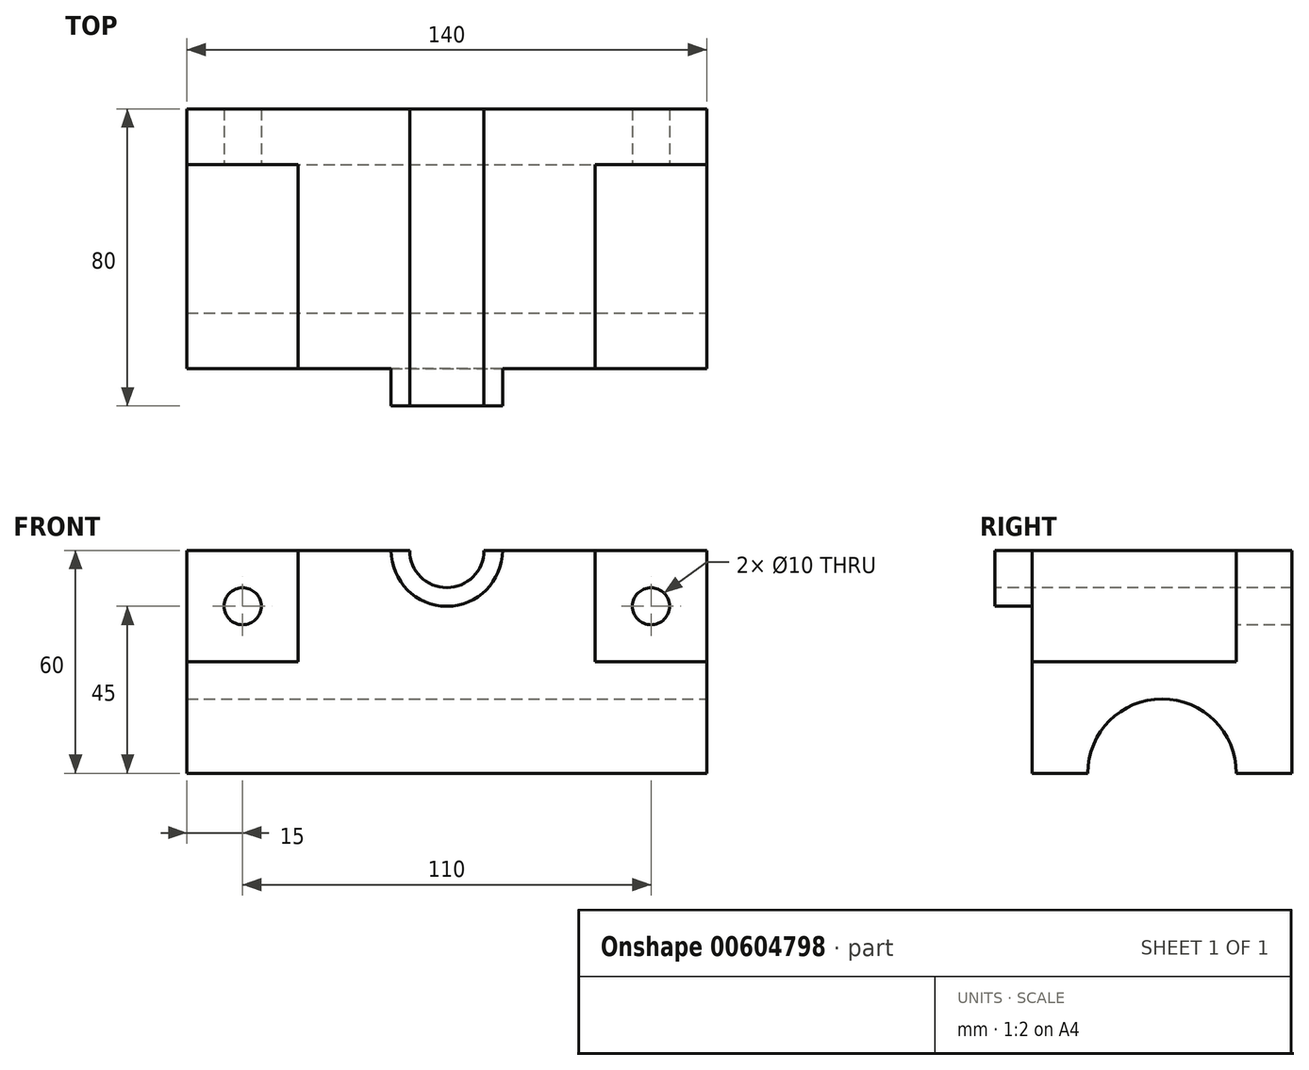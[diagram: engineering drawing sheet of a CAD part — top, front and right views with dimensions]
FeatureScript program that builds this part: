
annotation { "Feature Type Name" : "Feature", "Feature Type Description" : "" }
export const myFeature = defineFeature(function(context is Context, id is Id, definition is map)
    precondition{}
    {
        {
            var Q0;
            Q0=qCreatedBy(makeId("Front.planeOp"),FACE);
            var sketch = newSketch(context, id + "F0", { "sketchPlane" : qUnion([Q0])});
            skLineSegment(sketch, "E0.bottom", {"start": v(70, 30) * mm, "end": v(-70, 30) * mm});
            skLineSegment(sketch, "E0.top", {"start": v(70, -30) * mm, "end": v(-70, -30) * mm});
            skLineSegment(sketch, "E0.left", {"start": v(70, 30) * mm, "end": v(70, -30) * mm});
            skLineSegment(sketch, "E0.right", {"start": v(-70, 30) * mm, "end": v(-70, -30) * mm});
            skPoint(sketch, "E0.middle", {"position": v(0, 0) * mm});
            skSolve(sketch);
        }
        {
            var Q0;
            Q0=makeQuery(id+"F0.imprint","IMPRINT",FACE,{"disambiguationData":[TD([[makeQuery(id+"F0.imprint","IMPRINT",EDGE,{"derivedFrom":sQuery(id+"F0.wireOp",EDGE,"E0.bottom")}),1.0]])]});
            extrude(context, id + "F1", {"entities" : qUnion([Q0]), "depth" : 70 * mm, "offsetDistance" : 25 * mm});
        }
        {
            var Q0;
            Q0=makeQuery(id+"F1.opExtrude","SWEPT_FACE",FACE,{"disambiguationData":[OSD([sQuery(id+"F0.wireOp",EDGE,"E0.left")])]});
            var sketch = newSketch(context, id + "F2", { "sketchPlane" : qUnion([Q0])});
            skArc(sketch, "E1", {"start": v(-15, -30) * mm, "mid": v(-35, -10) * mm, "end": v(-55, -30) * mm});
            skSolve(sketch);
        }
        {
            var Q0;
            {var subQ0=sQuery(id+"F2.wireOp",EDGE,"E1");Q0=makeQuery(id+"F2.imprint","IMPRINT",FACE,{"disambiguationData":[TD([[makeQuery(id+"F2.imprint","IMPRINT",EDGE,{"derivedFrom":subQ0}),1.0]])]});}
            extrude(context, id + "F3", {"entities" : qUnion([Q0]), "operationType" : NewBodyOperationType.REMOVE, "oppositeDirection" : true, "depth" : 330 * mm, "offsetDistance" : 25 * mm, "symmetric" : true});
        }
        {
            var Q0;
            Q0=makeQuery(id+"F1.opExtrude","CAP_FACE",FACE,{"disambiguationData":[OSD([sQuery(id+"F0.wireOp",EDGE,"E0.bottom"),sQuery(id+"F0.wireOp",EDGE,"E0.top"),sQuery(id+"F0.wireOp",EDGE,"E0.left"),sQuery(id+"F0.wireOp",EDGE,"E0.right")])],"isStart":false});
            var sketch = newSketch(context, id + "F4", { "sketchPlane" : qUnion([Q0])});
            skLineSegment(sketch, "E2", {"start": v(40, 30) * mm, "end": v(40, 0) * mm});
            skLineSegment(sketch, "E3", {"start": v(40, 0) * mm, "end": v(70, 0) * mm});
            skLineSegment(sketch, "E4", {"start": v(40, 30) * mm, "end": v(70, 30) * mm});
            skLineSegment(sketch, "E5", {"start": v(70, 30) * mm, "end": v(70, 0) * mm});
            skSolve(sketch);
        }
        {
            var Q0;
            Q0=makeQuery(id+"F4.imprint","IMPRINT",FACE,{"disambiguationData":[TD([[makeQuery(id+"F4.imprint","IMPRINT",EDGE,{"derivedFrom":sQuery(id+"F4.wireOp",EDGE,"E2")}),1.0]])]});
            extrude(context, id + "F5", {"entities" : qUnion([Q0]), "operationType" : NewBodyOperationType.REMOVE, "oppositeDirection" : true, "depth" : 55 * mm, "offsetDistance" : 25 * mm});
        }
        {
            var Q0;
            Q0=makeQuery(id+"F1.opExtrude","CAP_FACE",FACE,{"disambiguationData":[OSD([sQuery(id+"F0.wireOp",EDGE,"E0.bottom"),sQuery(id+"F0.wireOp",EDGE,"E0.top"),sQuery(id+"F0.wireOp",EDGE,"E0.left"),sQuery(id+"F0.wireOp",EDGE,"E0.right")])],"isStart":false});
            var sketch = newSketch(context, id + "F6", { "sketchPlane" : qUnion([Q0])});
            skLineSegment(sketch, "E6", {"start": v(-70, 0) * mm, "end": v(-40, 0) * mm});
            skLineSegment(sketch, "E7", {"start": v(-40, 0) * mm, "end": v(-40, 30) * mm});
            skLineSegment(sketch, "E8", {"start": v(-40, 30) * mm, "end": v(-70, 30) * mm});
            skLineSegment(sketch, "E9", {"start": v(-70, 30) * mm, "end": v(-70, 0) * mm});
            skSolve(sketch);
        }
        {
            var Q0;
            Q0=makeQuery(id+"F6.imprint","IMPRINT",FACE,{"disambiguationData":[TD([[makeQuery(id+"F6.imprint","IMPRINT",EDGE,{"derivedFrom":sQuery(id+"F6.wireOp",EDGE,"E6")}),1.0]])]});
            extrude(context, id + "F7", {"entities" : qUnion([Q0]), "operationType" : NewBodyOperationType.REMOVE, "oppositeDirection" : true, "depth" : 55 * mm, "offsetDistance" : 25 * mm});
        }
        {
            var Q0;
            Q0=makeQuery(id+"F5.boolean.opBoolean","COPY",FACE,{"derivedFrom":makeQuery(id+"F5.opExtrude","CAP_FACE",FACE,{"disambiguationData":[OSD([sQuery(id+"F4.wireOp",EDGE,"E2"),sQuery(id+"F4.wireOp",EDGE,"E3"),sQuery(id+"F4.wireOp",EDGE,"E4"),sQuery(id+"F4.wireOp",EDGE,"E5")])],"isStart":false})});
            var sketch = newSketch(context, id + "F8", { "sketchPlane" : qUnion([Q0])});
            skCircle(sketch, "E10", {"center": v(55, 15) * mm, "radius": 5 * mm});
            skSolve(sketch);
        }
        {
            var Q0;
            Q0=makeQuery(id+"F8.imprint","IMPRINT",FACE,{"disambiguationData":[TD([[makeQuery(id+"F8.imprint","IMPRINT",EDGE,{"derivedFrom":sQuery(id+"F8.wireOp",EDGE,"E10")}),1.0]])]});
            extrude(context, id + "F9", {"entities" : qUnion([Q0]), "operationType" : NewBodyOperationType.REMOVE, "oppositeDirection" : true, "depth" : 40 * mm, "offsetDistance" : 25 * mm});
        }
        {
            var Q0;
            Q0=makeQuery(id+"F7.boolean.opBoolean","COPY",FACE,{"derivedFrom":makeQuery(id+"F7.opExtrude","CAP_FACE",FACE,{"disambiguationData":[OSD([sQuery(id+"F6.wireOp",EDGE,"E6"),sQuery(id+"F6.wireOp",EDGE,"E7"),sQuery(id+"F6.wireOp",EDGE,"E8"),sQuery(id+"F6.wireOp",EDGE,"E9")])],"isStart":false})});
            var sketch = newSketch(context, id + "F10", { "sketchPlane" : qUnion([Q0])});
            skCircle(sketch, "E11", {"center": v(-55, 15) * mm, "radius": 5 * mm});
            skSolve(sketch);
        }
        {
            var Q0;
            Q0=makeQuery(id+"F10.imprint","IMPRINT",FACE,{"disambiguationData":[TD([[makeQuery(id+"F10.imprint","IMPRINT",EDGE,{"derivedFrom":sQuery(id+"F10.wireOp",EDGE,"E11")}),1.0]])]});
            extrude(context, id + "F11", {"entities" : qUnion([Q0]), "operationType" : NewBodyOperationType.REMOVE, "oppositeDirection" : true, "depth" : 40 * mm, "offsetDistance" : 25 * mm});
        }
        {
            var Q0;
            Q0=makeQuery(id+"F1.opExtrude","CAP_FACE",FACE,{"disambiguationData":[OSD([sQuery(id+"F0.wireOp",EDGE,"E0.bottom"),sQuery(id+"F0.wireOp",EDGE,"E0.top"),sQuery(id+"F0.wireOp",EDGE,"E0.left"),sQuery(id+"F0.wireOp",EDGE,"E0.right")])],"isStart":false});
            var sketch = newSketch(context, id + "F12", { "sketchPlane" : qUnion([Q0])});
            skCircle(sketch, "E12", {"center": v(0, 30) * mm, "radius": 10 * mm});
            skCircle(sketch, "E13", {"center": v(0, 30) * mm, "radius": 15 * mm});
            skSolve(sketch);
        }
        {
            var Q0;
            {var subQ0=sQuery(id+"F12.wireOp",EDGE,"E12");var subQ1=makeQuery(id+"F1.opExtrude","CAP_EDGE",EDGE,{"disambiguationData":[OSD([sQuery(id+"F0.wireOp",EDGE,"E0.bottom")])],"isStart":false});var subQ2=makeQuery(id+"F12.imprint","INTERSECT",VERTEX,{"disambiguationData":[OD(0.0)],"derivedFrom":[subQ1,subQ0]});Q0=makeQuery(id+"F12.imprint","IMPRINT",FACE,{"disambiguationData":[TD([[makeQuery(id+"F12.imprint","IMPRINT",EDGE,{"disambiguationData":[TD([[subQ2,1.0]])],"derivedFrom":subQ0}),1.0]])]});}
            var Q1;
            {var subQ0=sQuery(id+"F12.wireOp",EDGE,"E12");var subQ1=makeQuery(id+"F1.opExtrude","CAP_EDGE",EDGE,{"disambiguationData":[OSD([sQuery(id+"F0.wireOp",EDGE,"E0.bottom")])],"isStart":false});var subQ2=makeQuery(id+"F12.imprint","INTERSECT",VERTEX,{"disambiguationData":[OD(0.0)],"derivedFrom":[subQ1,subQ0]});Q1=makeQuery(id+"F12.imprint","IMPRINT",FACE,{"disambiguationData":[TD([[makeQuery(id+"F12.imprint","IMPRINT",EDGE,{"disambiguationData":[TD([[subQ2,-1.0]])],"derivedFrom":subQ0}),1.0]])]});}
            var Q2;
            {var subQ0=sQuery(id+"F12.wireOp",EDGE,"E12");var subQ1=makeQuery(id+"F1.opExtrude","CAP_EDGE",EDGE,{"disambiguationData":[OSD([sQuery(id+"F0.wireOp",EDGE,"E0.bottom")])],"isStart":false});var subQ2=makeQuery(id+"F12.imprint","INTERSECT",VERTEX,{"disambiguationData":[OD(0.0)],"derivedFrom":[subQ1,subQ0]});Q2=makeQuery(id+"F12.imprint","IMPRINT",FACE,{"disambiguationData":[TD([[makeQuery(id+"F12.imprint","IMPRINT",EDGE,{"disambiguationData":[TD([[subQ2,-1.0]])],"derivedFrom":subQ0}),-1.0]])]});}
            extrude(context, id + "F13", {"entities" : qUnion([Q0, Q1, Q2]), "operationType" : NewBodyOperationType.REMOVE, "oppositeDirection" : true, "depth" : 100 * mm, "offsetDistance" : 25 * mm});
        }
        {
            var Q0;
            {var subQ0=sQuery(id+"F12.wireOp",EDGE,"E12");var subQ1=makeQuery(id+"F1.opExtrude","CAP_EDGE",EDGE,{"disambiguationData":[OSD([sQuery(id+"F0.wireOp",EDGE,"E0.bottom")])],"isStart":false});var subQ2=makeQuery(id+"F12.imprint","INTERSECT",VERTEX,{"disambiguationData":[OD(0.0)],"derivedFrom":[subQ1,subQ0]});Q0=makeQuery(id+"F12.imprint","IMPRINT",FACE,{"disambiguationData":[TD([[makeQuery(id+"F12.imprint","IMPRINT",EDGE,{"disambiguationData":[TD([[subQ2,1.0]])],"derivedFrom":subQ0}),-1.0]])]});}
            extrude(context, id + "F14", {"entities" : qUnion([Q0]), "operationType" : NewBodyOperationType.ADD, "depth" : 10 * mm, "offsetDistance" : 25 * mm});
        }
    });
